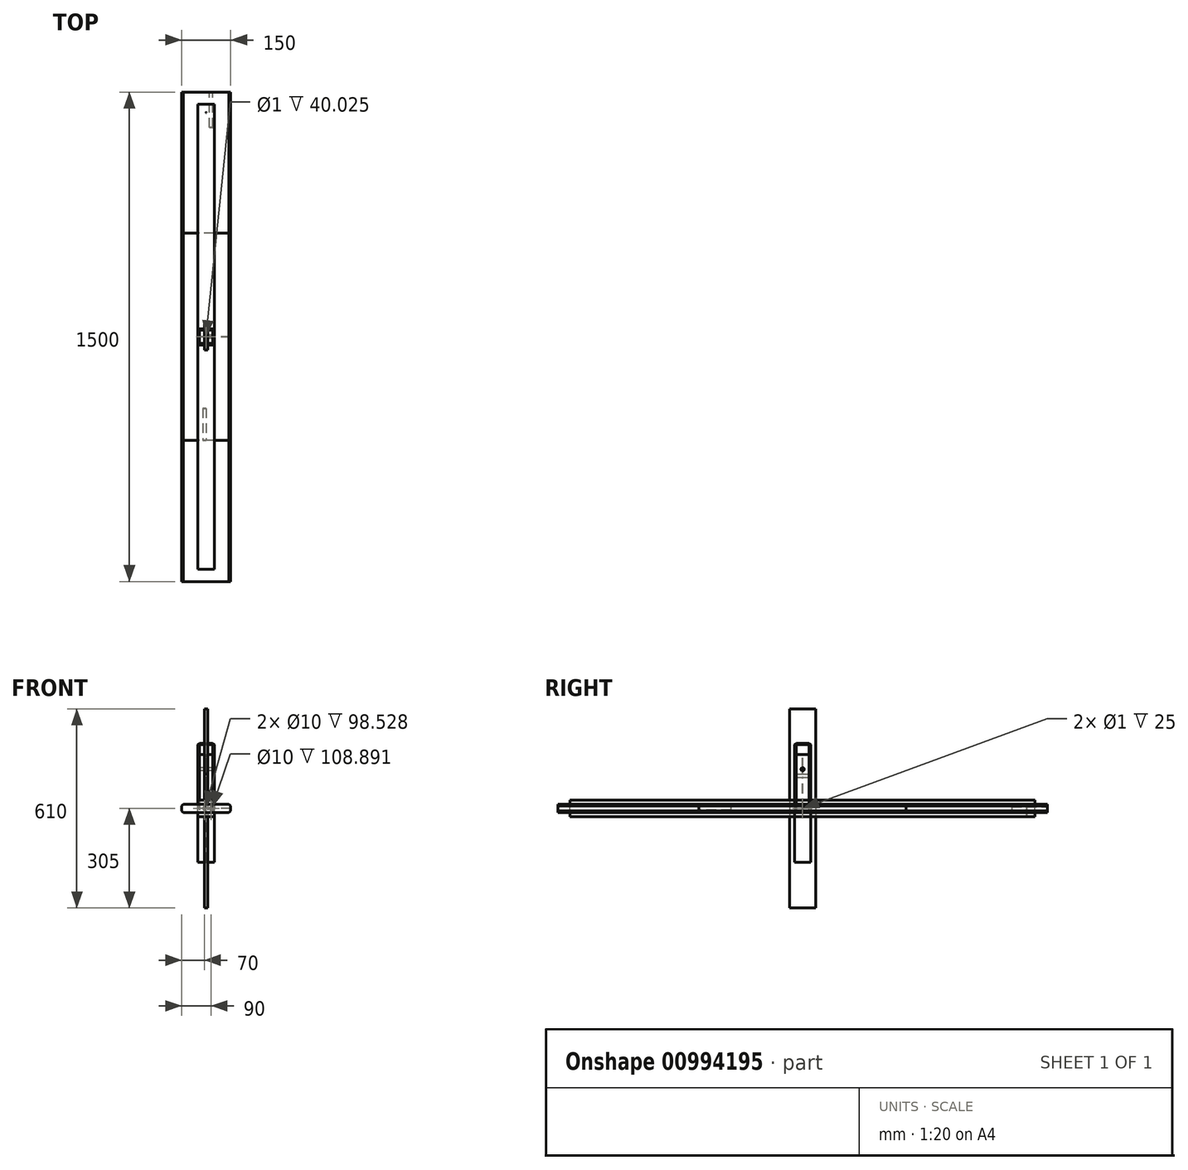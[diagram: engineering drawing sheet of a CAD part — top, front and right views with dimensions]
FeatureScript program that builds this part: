
annotation { "Feature Type Name" : "Feature", "Feature Type Description" : "" }
export const myFeature = defineFeature(function(context is Context, id is Id, definition is map)
    precondition{}
    {
        {
            var Q0;
            Q0=qCreatedBy(makeId("Top.planeOp"),FACE);
            var sketch = newSketch(context, id + "F0", { "sketchPlane" : qUnion([Q0])});
            skLineSegment(sketch, "E0.bottom", {"start": v(-25, -25) * mm, "end": v(25, -25) * mm});
            skLineSegment(sketch, "E0.top", {"start": v(-25, 25) * mm, "end": v(25, 25) * mm});
            skLineSegment(sketch, "E0.left", {"start": v(-25, -25) * mm, "end": v(-25, 25) * mm});
            skLineSegment(sketch, "E0.right", {"start": v(25, -25) * mm, "end": v(25, 25) * mm});
            skPoint(sketch, "E0.middle", {"position": v(0, 0) * mm});
            skSolve(sketch);
        }
        {
            var Q0;
            Q0 = qSketchRegion(id + "F0", true);
            extrude(context, id + "F1", {"entities" : qUnion([Q0]), "endBound" : BoundingType.SYMMETRIC, "depth" : 400 * mm, "offsetDistance" : 25 * mm});
        }
        {
            var Q0;
            Q0=makeQuery(id+"F1.opExtrude","SWEPT_EDGE",EDGE,{"disambiguationData":[OSD([sQuery(id+"F0.wireOp",EDGE,"E0.bottom"),sQuery(id+"F0.wireOp",EDGE,"E0.left")])]});
            var Q1;
            Q1=makeQuery(id+"F1.opExtrude","SWEPT_EDGE",EDGE,{"disambiguationData":[OSD([sQuery(id+"F0.wireOp",EDGE,"E0.bottom"),sQuery(id+"F0.wireOp",EDGE,"E0.right")])]});
            var Q2;
            Q2=makeQuery(id+"F1.opExtrude","SWEPT_EDGE",EDGE,{"disambiguationData":[OSD([sQuery(id+"F0.wireOp",EDGE,"E0.top"),sQuery(id+"F0.wireOp",EDGE,"E0.left")])]});
            var Q3;
            Q3=makeQuery(id+"F1.opExtrude","SWEPT_EDGE",EDGE,{"disambiguationData":[OSD([sQuery(id+"F0.wireOp",EDGE,"E0.top"),sQuery(id+"F0.wireOp",EDGE,"E0.right")])]});
            var Q4;
            Q4=makeQuery(id+"F1.opExtrude","CAP_FACE",FACE,{"disambiguationData":[OSD([sQuery(id+"F0.wireOp",EDGE,"E0.bottom"),sQuery(id+"F0.wireOp",EDGE,"E0.top"),sQuery(id+"F0.wireOp",EDGE,"E0.left"),sQuery(id+"F0.wireOp",EDGE,"E0.right")])],"isStart":false});
            var Q5;
            Q5=makeQuery(id+"F1.opExtrude","CAP_FACE",FACE,{"disambiguationData":[OSD([sQuery(id+"F0.wireOp",EDGE,"E0.bottom"),sQuery(id+"F0.wireOp",EDGE,"E0.top"),sQuery(id+"F0.wireOp",EDGE,"E0.left"),sQuery(id+"F0.wireOp",EDGE,"E0.right")])],"isStart":true});
            chamfer(context, id + "F2", {"entities" : qUnion([Q0, Q1, Q2, Q3, Q4, Q5]), "width" : 5 * mm, "tangentPropagation" : true});
        }
        {
            var Q0;
            Q0=makeQuery(id+"F1.opExtrude","SWEPT_FACE",FACE,{"disambiguationData":[OSD([sQuery(id+"F0.wireOp",EDGE,"E0.left")])]});
            var sketch = newSketch(context, id + "F3", { "sketchPlane" : qUnion([Q0])});
            skCircle(sketch, "E1", {"center": v(0, 120) * mm, "radius": 5 * mm});
            skSolve(sketch);
        }
        {
            var Q0;
            Q0 = qSketchRegion(id + "F3", true);
            extrude(context, id + "F4", {"entities" : qUnion([Q0]), "operationType" : NewBodyOperationType.REMOVE, "oppositeDirection" : true, "depth" : 87.4 * mm, "offsetDistance" : 25 * mm});
        }
        {
            var Q0;
            Q0=makeQuery(id+"F1.opExtrude","SWEPT_FACE",FACE,{"disambiguationData":[OSD([sQuery(id+"F0.wireOp",EDGE,"E0.top")])]});
            var sketch = newSketch(context, id + "F5", { "sketchPlane" : qUnion([Q0])});
            skCircle(sketch, "E2", {"center": v(0, 100) * mm, "radius": 5 * mm});
            skSolve(sketch);
        }
        {
            var Q0;
            Q0=makeQuery(id+"F5.imprint","IMPRINT",FACE,{"disambiguationData":[TD([[makeQuery(id+"F5.imprint","IMPRINT",EDGE,{"derivedFrom":sQuery(id+"F5.wireOp",EDGE,"E2")}),1.0]])]});
            var Q1;
            Q1=makeQuery(id+"F1.opExtrude","SWEPT_BODY",BODY,{"disambiguationData":[OSD([sQuery(id+"F0.wireOp",EDGE,"E0.bottom"),sQuery(id+"F0.wireOp",EDGE,"E0.top"),sQuery(id+"F0.wireOp",EDGE,"E0.left"),sQuery(id+"F0.wireOp",EDGE,"E0.right")])]});
            extrude(context, id + "F6", {"entities" : qUnion([Q0]), "operationType" : NewBodyOperationType.REMOVE, "endBound" : BoundingType.UP_TO_BODY, "oppositeDirection" : true, "depth" : 25 * mm, "endBoundEntityBody" : qUnion([Q1]), "offsetDistance" : 25 * mm});
        }
        {
            var Q0;
            Q0=qCreatedBy(makeId("Front.planeOp"),FACE);
            var sketch = newSketch(context, id + "F7", { "sketchPlane" : qUnion([Q0])});
            skLineSegment(sketch, "E3.bottom", {"start": v(75, 12.5) * mm, "end": v(-75, 12.5) * mm});
            skLineSegment(sketch, "E3.top", {"start": v(75, -12.5) * mm, "end": v(-75, -12.5) * mm});
            skLineSegment(sketch, "E3.left", {"start": v(75, 12.5) * mm, "end": v(75, -12.5) * mm});
            skLineSegment(sketch, "E3.right", {"start": v(-75, 12.5) * mm, "end": v(-75, -12.5) * mm});
            skPoint(sketch, "E3.middle", {"position": v(0, 0) * mm});
            skSolve(sketch);
        }
        {
            var Q0;
            Q0 = qSketchRegion(id + "F7", true);
            extrude(context, id + "F8", {"entities" : qUnion([Q0]), "endBound" : BoundingType.SYMMETRIC, "depth" : 1500 * mm, "offsetDistance" : 25 * mm});
        }
        {
            var Q0;
            Q0=makeQuery(id+"F8.opExtrude","SWEPT_EDGE",EDGE,{"disambiguationData":[OSD([sQuery(id+"F7.wireOp",EDGE,"E3.bottom"),sQuery(id+"F7.wireOp",EDGE,"E3.left")])]});
            var Q1;
            Q1=makeQuery(id+"F8.opExtrude","SWEPT_EDGE",EDGE,{"disambiguationData":[OSD([sQuery(id+"F7.wireOp",EDGE,"E3.top"),sQuery(id+"F7.wireOp",EDGE,"E3.right")])]});
            var Q2;
            Q2=makeQuery(id+"F8.opExtrude","SWEPT_EDGE",EDGE,{"disambiguationData":[OSD([sQuery(id+"F7.wireOp",EDGE,"E3.top"),sQuery(id+"F7.wireOp",EDGE,"E3.left")])]});
            var Q3;
            Q3=makeQuery(id+"F8.opExtrude","SWEPT_EDGE",EDGE,{"disambiguationData":[OSD([sQuery(id+"F7.wireOp",EDGE,"E3.bottom"),sQuery(id+"F7.wireOp",EDGE,"E3.right")])]});
            chamfer(context, id + "F9", {"entities" : qUnion([Q0, Q1, Q2, Q3]), "width" : 5 * mm, "tangentPropagation" : true});
        }
        {
            var Q0;
            Q0=makeQuery(id+"F8.opExtrude","CAP_FACE",FACE,{"disambiguationData":[OSD([sQuery(id+"F7.wireOp",EDGE,"E3.bottom"),sQuery(id+"F7.wireOp",EDGE,"E3.top"),sQuery(id+"F7.wireOp",EDGE,"E3.left"),sQuery(id+"F7.wireOp",EDGE,"E3.right")])],"isStart":true});
            var sketch = newSketch(context, id + "F10", { "sketchPlane" : qUnion([Q0])});
            skCircle(sketch, "E4", {"center": v(-15, 0) * mm, "radius": 5 * mm});
            skSolve(sketch);
        }
        {
            var Q0;
            Q0 = qSketchRegion(id + "F10", true);
            extrude(context, id + "F11", {"entities" : qUnion([Q0]), "operationType" : NewBodyOperationType.REMOVE, "oppositeDirection" : true, "depth" : 108.9 * mm, "offsetDistance" : 25 * mm});
        }
        {
            var Q0;
            Q0=makeQuery(id+"F8.opExtrude","SWEPT_FACE",FACE,{"disambiguationData":[OSD([sQuery(id+"F7.wireOp",EDGE,"E3.bottom")])]});
            var sketch = newSketch(context, id + "F12", { "sketchPlane" : qUnion([Q0])});
            skCircle(sketch, "E5", {"center": v(0, 0) * mm, "radius": 0.5 * mm});
            skSolve(sketch);
        }
        {
            var Q0;
            Q0=makeQuery(id+"F12.imprint","IMPRINT",FACE,{"disambiguationData":[TD([[makeQuery(id+"F12.imprint","IMPRINT",EDGE,{"derivedFrom":sQuery(id+"F12.wireOp",EDGE,"E5")}),1.0]])]});
            var Q1;
            Q1=makeQuery(id+"F8.opExtrude","SWEPT_FACE",FACE,{"disambiguationData":[OSD([sQuery(id+"F7.wireOp",EDGE,"E3.top")])]});
            extrude(context, id + "F13", {"entities" : qUnion([Q0, Q1]), "operationType" : NewBodyOperationType.REMOVE, "endBound" : BoundingType.THROUGH_ALL, "oppositeDirection" : true, "depth" : 25 * mm, "offsetDistance" : 25 * mm});
        }
        {
            var Q0;
            Q0=qCreatedBy(makeId("Front.planeOp"),FACE);
            var sketch = newSketch(context, id + "F14", { "sketchPlane" : qUnion([Q0])});
            skLineSegment(sketch, "E6.bottom", {"start": v(75, 12.5) * mm, "end": v(-75, 12.5) * mm});
            skLineSegment(sketch, "E6.top", {"start": v(75, -12.5) * mm, "end": v(-75, -12.5) * mm});
            skLineSegment(sketch, "E6.left", {"start": v(75, 12.5) * mm, "end": v(75, -12.5) * mm});
            skLineSegment(sketch, "E6.right", {"start": v(-75, 12.5) * mm, "end": v(-75, -12.5) * mm});
            skPoint(sketch, "E6.middle", {"position": v(0, 0) * mm});
            skSolve(sketch);
        }
        {
            var Q0;
            Q0 = qSketchRegion(id + "F14", true);
            extrude(context, id + "F15", {"entities" : qUnion([Q0]), "endBound" : BoundingType.SYMMETRIC, "depth" : 635 * mm, "offsetDistance" : 25 * mm});
        }
        {
            var Q0;
            Q0=makeQuery(id+"F15.opExtrude","SWEPT_EDGE",EDGE,{"disambiguationData":[OSD([sQuery(id+"F14.wireOp",EDGE,"E6.bottom"),sQuery(id+"F14.wireOp",EDGE,"E6.left")])]});
            var Q1;
            Q1=makeQuery(id+"F15.opExtrude","SWEPT_EDGE",EDGE,{"disambiguationData":[OSD([sQuery(id+"F14.wireOp",EDGE,"E6.top"),sQuery(id+"F14.wireOp",EDGE,"E6.left")])]});
            var Q2;
            Q2=makeQuery(id+"F15.opExtrude","SWEPT_EDGE",EDGE,{"disambiguationData":[OSD([sQuery(id+"F14.wireOp",EDGE,"E6.bottom"),sQuery(id+"F14.wireOp",EDGE,"E6.right")])]});
            var Q3;
            Q3=makeQuery(id+"F15.opExtrude","SWEPT_EDGE",EDGE,{"disambiguationData":[OSD([sQuery(id+"F14.wireOp",EDGE,"E6.top"),sQuery(id+"F14.wireOp",EDGE,"E6.right")])]});
            chamfer(context, id + "F16", {"entities" : qUnion([Q0, Q1, Q2, Q3]), "width" : 5 * mm, "tangentPropagation" : true});
        }
        {
            var Q0;
            Q0=makeQuery(id+"F15.opExtrude","CAP_FACE",FACE,{"disambiguationData":[OSD([sQuery(id+"F14.wireOp",EDGE,"E6.bottom"),sQuery(id+"F14.wireOp",EDGE,"E6.top"),sQuery(id+"F14.wireOp",EDGE,"E6.left"),sQuery(id+"F14.wireOp",EDGE,"E6.right")])],"isStart":false});
            var sketch = newSketch(context, id + "F17", { "sketchPlane" : qUnion([Q0])});
            skCircle(sketch, "E7", {"center": v(-5, 0) * mm, "radius": 5 * mm});
            skSolve(sketch);
        }
        {
            var Q0;
            Q0 = qSketchRegion(id + "F17", true);
            extrude(context, id + "F18", {"entities" : qUnion([Q0]), "operationType" : NewBodyOperationType.REMOVE, "oppositeDirection" : true, "depth" : 98.53 * mm, "offsetDistance" : 25 * mm});
        }
        {
            var Q0;
            Q0=qCreatedBy(makeId("Front.planeOp"),FACE);
            var sketch = newSketch(context, id + "F19", { "sketchPlane" : qUnion([Q0])});
            skLineSegment(sketch, "E8.bottom", {"start": v(25, -25) * mm, "end": v(-25, -25) * mm});
            skLineSegment(sketch, "E8.top", {"start": v(25, 25) * mm, "end": v(-25, 25) * mm});
            skLineSegment(sketch, "E8.left", {"start": v(25, -25) * mm, "end": v(25, 25) * mm});
            skLineSegment(sketch, "E8.right", {"start": v(-25, -25) * mm, "end": v(-25, 25) * mm});
            skPoint(sketch, "E8.middle", {"position": v(0, 0) * mm});
            skSolve(sketch);
        }
        {
            var Q0;
            Q0 = qSketchRegion(id + "F19", true);
            extrude(context, id + "F20", {"entities" : qUnion([Q0]), "endBound" : BoundingType.SYMMETRIC, "depth" : 1425 * mm, "offsetDistance" : 25 * mm});
        }
        {
            var Q0;
            Q0=makeQuery(id+"F20.opExtrude","SWEPT_FACE",FACE,{"disambiguationData":[OSD([sQuery(id+"F19.wireOp",EDGE,"E8.right")])]});
            var sketch = newSketch(context, id + "F21", { "sketchPlane" : qUnion([Q0])});
            skCircle(sketch, "E9", {"center": v(0, 0) * mm, "radius": 0.5 * mm});
            skSolve(sketch);
        }
        {
            var Q0;
            Q0 = qSketchRegion(id + "F21", true);
            extrude(context, id + "F22", {"entities" : qUnion([Q0]), "operationType" : NewBodyOperationType.REMOVE, "endBound" : BoundingType.THROUGH_ALL, "oppositeDirection" : true, "depth" : 25 * mm, "offsetDistance" : 25 * mm});
        }
        {
            var Q0;
            Q0=makeQuery(id+"F20.opExtrude","SWEPT_FACE",FACE,{"disambiguationData":[OSD([sQuery(id+"F19.wireOp",EDGE,"E8.top")])]});
            var sketch = newSketch(context, id + "F23", { "sketchPlane" : qUnion([Q0])});
            skCircle(sketch, "E10", {"center": v(0, 687.5) * mm, "radius": 0.5 * mm});
            skSolve(sketch);
        }
        {
            var Q0;
            Q0 = qSketchRegion(id + "F23", true);
            extrude(context, id + "F24", {"entities" : qUnion([Q0]), "operationType" : NewBodyOperationType.REMOVE, "endBound" : BoundingType.THROUGH_ALL, "oppositeDirection" : true, "depth" : 25 * mm, "offsetDistance" : 25 * mm});
        }
        {
            var Q0;
            Q0=qCreatedBy(makeId("Top.planeOp"),FACE);
            var sketch = newSketch(context, id + "F25", { "sketchPlane" : qUnion([Q0])});
            skLineSegment(sketch, "E11.bottom", {"start": v(-25, -25) * mm, "end": v(25, -25) * mm});
            skLineSegment(sketch, "E11.top", {"start": v(-25, 25) * mm, "end": v(25, 25) * mm});
            skLineSegment(sketch, "E11.left", {"start": v(-25, -25) * mm, "end": v(-25, 25) * mm});
            skLineSegment(sketch, "E11.right", {"start": v(25, -25) * mm, "end": v(25, 25) * mm});
            skPoint(sketch, "E11.middle", {"position": v(0, 0) * mm});
            skSolve(sketch);
        }
        {
            var Q0;
            Q0=makeQuery(id+"F25.imprint","IMPRINT",FACE,{"disambiguationData":[TD([[makeQuery(id+"F25.imprint","IMPRINT",EDGE,{"derivedFrom":sQuery(id+"F25.wireOp",EDGE,"E11.bottom")}),1.0]])]});
            extrude(context, id + "F26", {"entities" : qUnion([Q0]), "endBound" : BoundingType.SYMMETRIC, "depth" : 330 * mm, "offsetDistance" : 25 * mm});
        }
        {
            var Q0;
            Q0=makeQuery(id+"F26.opExtrude","CAP_FACE",FACE,{"disambiguationData":[OSD([sQuery(id+"F25.wireOp",EDGE,"E11.bottom"),sQuery(id+"F25.wireOp",EDGE,"E11.top"),sQuery(id+"F25.wireOp",EDGE,"E11.left"),sQuery(id+"F25.wireOp",EDGE,"E11.right")])],"isStart":false});
            var sketch = newSketch(context, id + "F27", { "sketchPlane" : qUnion([Q0])});
            skCircle(sketch, "E12", {"center": v(0, 0) * mm, "radius": 0.5 * mm});
            skSolve(sketch);
        }
        {
            var Q0;
            Q0=makeQuery(id+"F27.imprint","IMPRINT",FACE,{"disambiguationData":[TD([[makeQuery(id+"F27.imprint","IMPRINT",EDGE,{"derivedFrom":sQuery(id+"F27.wireOp",EDGE,"E12")}),1.0]])]});
            extrude(context, id + "F28", {"entities" : qUnion([Q0]), "operationType" : NewBodyOperationType.REMOVE, "endBound" : BoundingType.THROUGH_ALL, "oppositeDirection" : true, "depth" : 25 * mm, "offsetDistance" : 25 * mm});
        }
        {
            var Q0;
            Q0=qCreatedBy(makeId("Top.planeOp"),FACE);
            var sketch = newSketch(context, id + "F29", { "sketchPlane" : qUnion([Q0])});
            skLineSegment(sketch, "E13.bottom", {"start": v(-5, -40) * mm, "end": v(5, -40) * mm});
            skLineSegment(sketch, "E13.top", {"start": v(-5, 40) * mm, "end": v(5, 40) * mm});
            skLineSegment(sketch, "E13.left", {"start": v(5, -40) * mm, "end": v(5, 40) * mm});
            skLineSegment(sketch, "E13.right", {"start": v(-5, -40) * mm, "end": v(-5, 40) * mm});
            skPoint(sketch, "E13.middle", {"position": v(0, 0) * mm});
            skSolve(sketch);
        }
        {
            var Q0;
            Q0=makeQuery(id+"F29.imprint","IMPRINT",FACE,{"disambiguationData":[TD([[makeQuery(id+"F29.imprint","IMPRINT",EDGE,{"derivedFrom":sQuery(id+"F29.wireOp",EDGE,"E13.bottom")}),1.0]])]});
            extrude(context, id + "F30", {"entities" : qUnion([Q0]), "endBound" : BoundingType.SYMMETRIC, "depth" : 610 * mm, "offsetDistance" : 25 * mm});
        }
    });
